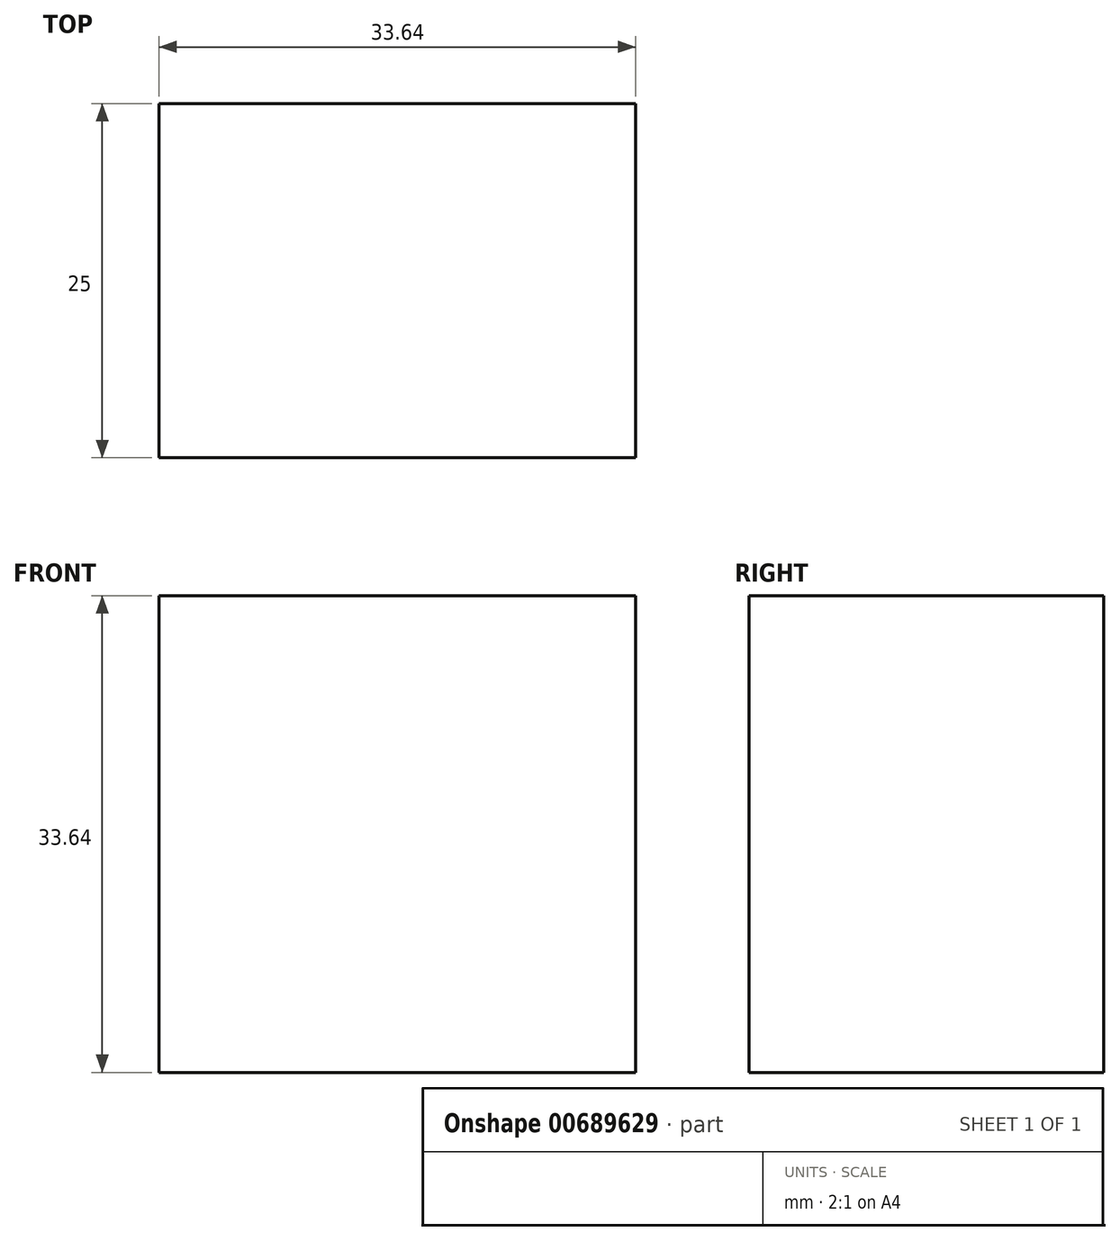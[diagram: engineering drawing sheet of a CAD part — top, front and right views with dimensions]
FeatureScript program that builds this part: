
annotation { "Feature Type Name" : "Feature", "Feature Type Description" : "" }
export const myFeature = defineFeature(function(context is Context, id is Id, definition is map)
    precondition{}
    {
        {
            var Q0;
            Q0=qCreatedBy(makeId("Front.planeOp"),FACE);
            var sketch = newSketch(context, id + "F0", { "sketchPlane" : qUnion([Q0])});
            skLineSegment(sketch, "E0.bottom", {"start": v(0, 0) * mm, "end": v(-80, 0) * mm});
            skLineSegment(sketch, "E0.top", {"start": v(0, 80) * mm, "end": v(-80, 80) * mm});
            skLineSegment(sketch, "E0.left", {"start": v(0, 0) * mm, "end": v(0, 80) * mm});
            skLineSegment(sketch, "E0.right", {"start": v(-80, 0) * mm, "end": v(-80, 80) * mm});
            skLineSegment(sketch, "E1.bottom", {"start": v(-46.36, 46.36) * mm, "end": v(-80, 46.36) * mm});
            skLineSegment(sketch, "E1.top", {"start": v(-46.36, 80) * mm, "end": v(-80, 80) * mm});
            skLineSegment(sketch, "E1.left", {"start": v(-46.36, 46.36) * mm, "end": v(-46.36, 80) * mm});
            skLineSegment(sketch, "E1.right", {"start": v(-80, 46.36) * mm, "end": v(-80, 80) * mm});
            skLineSegment(sketch, "E2.bottom", {"start": v(0, 80) * mm, "end": v(-33.64, 80) * mm});
            skLineSegment(sketch, "E2.top", {"start": v(0, 46.36) * mm, "end": v(-33.64, 46.36) * mm});
            skLineSegment(sketch, "E2.left", {"start": v(0, 80) * mm, "end": v(0, 46.36) * mm});
            skLineSegment(sketch, "E2.right", {"start": v(-33.64, 80) * mm, "end": v(-33.64, 46.36) * mm});
            skLineSegment(sketch, "E3.bottom", {"start": v(-80, 0) * mm, "end": v(-46.36, 0) * mm});
            skLineSegment(sketch, "E3.top", {"start": v(-80, 33.64) * mm, "end": v(-46.36, 33.64) * mm});
            skLineSegment(sketch, "E3.left", {"start": v(-80, 0) * mm, "end": v(-80, 33.64) * mm});
            skLineSegment(sketch, "E3.right", {"start": v(-46.36, 0) * mm, "end": v(-46.36, 33.64) * mm});
            skLineSegment(sketch, "E4.bottom", {"start": v(0, 0) * mm, "end": v(-33.64, 0) * mm});
            skLineSegment(sketch, "E4.top", {"start": v(0, 33.64) * mm, "end": v(-33.64, 33.64) * mm});
            skLineSegment(sketch, "E4.left", {"start": v(0, 0) * mm, "end": v(0, 33.64) * mm});
            skLineSegment(sketch, "E4.right", {"start": v(-33.64, 0) * mm, "end": v(-33.64, 33.64) * mm});
            skSolve(sketch);
        }
        {
            var Q0;
            Q0=makeQuery(id+"F0.imprint","IMPRINT",FACE,{"disambiguationData":[TD([[makeQuery(id+"F0.imprint","IMPRINT",EDGE,{"derivedFrom":sQuery(id+"F0.wireOp",EDGE,"E1.bottom")}),-1.0]])]});
            var Q1;
            Q1=makeQuery(id+"F0.imprint","IMPRINT",FACE,{"disambiguationData":[TD([[makeQuery(id+"F0.imprint","IMPRINT",EDGE,{"derivedFrom":sQuery(id+"F0.wireOp",EDGE,"E2.bottom")}),1.0]])]});
            var Q2;
            Q2=makeQuery(id+"F0.imprint","IMPRINT",FACE,{"disambiguationData":[TD([[makeQuery(id+"F0.imprint","IMPRINT",EDGE,{"derivedFrom":sQuery(id+"F0.wireOp",EDGE,"E3.bottom")}),1.0]])]});
            var Q3;
            Q3=makeQuery(id+"F0.imprint","IMPRINT",FACE,{"disambiguationData":[TD([[makeQuery(id+"F0.imprint","IMPRINT",EDGE,{"derivedFrom":sQuery(id+"F0.wireOp",EDGE,"E4.bottom")}),-1.0]])]});
            extrude(context, id + "F1", {"entities" : qUnion([Q0, Q1, Q2, Q3]), "depth" : 25 * mm, "offsetDistance" : 25 * mm});
        }
    });
